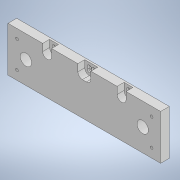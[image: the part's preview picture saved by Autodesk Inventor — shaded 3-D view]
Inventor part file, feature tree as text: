
AUTODESK INVENTOR PART (.ipt)
format: ipt  version: 2022 (Build 260153000, 153)  size: 255,488 bytes
history: native  units: in
note: dims shown in document units (in); Inventor stores cm internally (conversion verified against a paired STEP export)
features: sketch x6, extrude x3, hole x3, chamfer x3
ambient origin geometry x8: Origin, YZ Plane, XZ Plane, XY Plane, X Axis, Y Axis, Z Axis, Center Point
bodies: Solid1 (feature_tree)
feature tree (15):
  extrude  "Extrusion1"  Depth=0.9843in
  hole  "Hole1"  [1 undecoded]
  extrude  "Extrusion2"  Depth=2.5591in
  chamfer  "Chamfer1"  Distance=0.3937in
  hole  "Hole2"  [1 undecoded]
  extrude  "Extrusion3"  Depth=0.3937in
  chamfer  "Chamfer2"  Distance=3.3465in
  chamfer  "Chamfer3"  Distance=0.748in
  hole  "Hole3"  [1 undecoded]
  sketch  "Sketch1"  dims[d0=3.3465in d1=0.9843in]
  sketch  "Sketch2"  dims[d2=0.25in d3=0.0in d4=0.9843in]
  sketch  "Sketch3"  dims[d5=0.4921in d6=2.5591in]
  sketch  "Sketch4"  dims[d7=0.3937in]
  sketch  "Sketch5"  dims[d8=3.3465in]
  sketch  "Sketch6"  dims[d9=0.25in d10=0.75in d11=0.375in d12=0.25in d13=0.5635in d14=1.0in d15=0.8108in d16=0.3937in d17=0.3937in d18=1.8504in d19=3.3465in d20=0.748in d21=0.1575in d22=0.748in d23=0.9843in d24=0.1181in d25=0.0787in d26=0.1181in d27=0.1575in d28=0.1575in d29=0.0591in d30=0.0in d31=0.0197in d32=0.0787in d33=45.0deg d34=0.4616in d35=0.3374in d36=1.2333in d37=1.3219in d38=2.0935in d39=0.4656in d40=0.0472in d41=0.2362in d42=0.1575in d43=0.0787in d44=90.0deg d45=0.315in d46=0.8108in d47=0.1969in d48=0.1969in d49=0.0984in d50=0.0984in d51=0.1516in d52=0.0in d53=0.0197in d54=0.0787in d55=45.0deg d56=0.0591in d57=0.0197in d58=0.0787in d59=45.0deg d60=0.1969in d61=0.1969in d62=0.1969in d63=0.1969in d64=0.0617in d65=0.1575in d66=0.1575in d67=0.0787in d68=90.0deg d69=0.248in d70=0.8108in]
note: 3 required parameter values undecoded (feature->parameter linkage not recoverable at this tier; creation-order binding heuristic only, values carry confidence <= 0.55)
